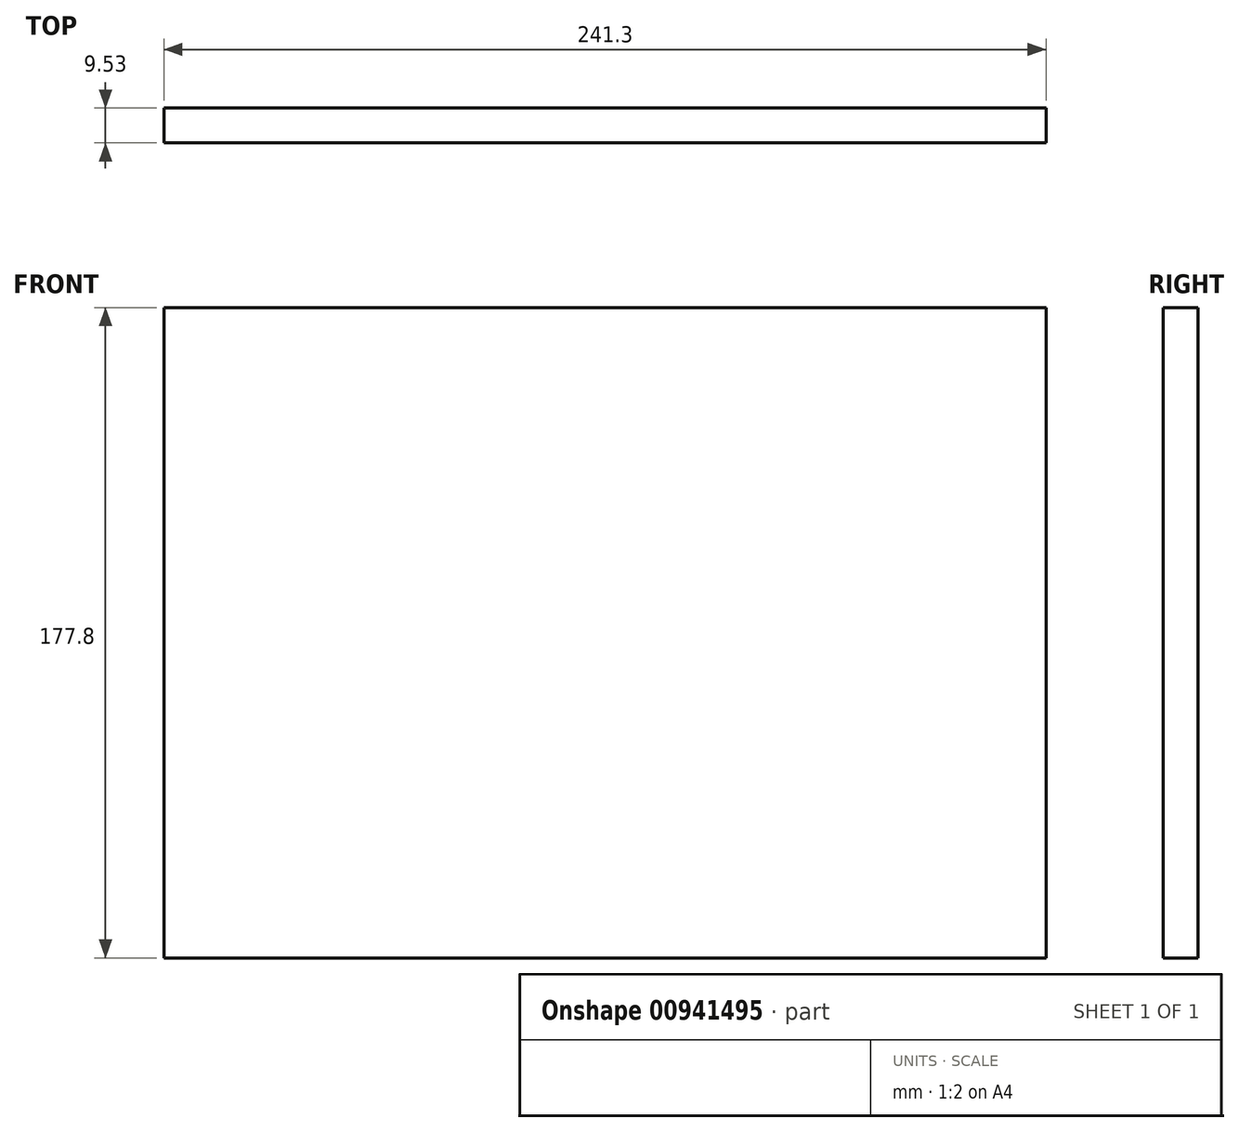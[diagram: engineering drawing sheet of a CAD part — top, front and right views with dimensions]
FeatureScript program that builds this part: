
annotation { "Feature Type Name" : "Feature", "Feature Type Description" : "" }
export const myFeature = defineFeature(function(context is Context, id is Id, definition is map)
    precondition{}
    {
        {
            var Q0;
            Q0=qCreatedBy(makeId("Front.planeOp"),FACE);
            var sketch = newSketch(context, id + "F0", { "sketchPlane" : qUnion([Q0])});
            skLineSegment(sketch, "E0.bottom", {"start": v(120.65, 88.9) * mm, "end": v(-120.65, 88.9) * mm});
            skLineSegment(sketch, "E0.top", {"start": v(120.65, -88.9) * mm, "end": v(-120.65, -88.9) * mm});
            skLineSegment(sketch, "E0.left", {"start": v(120.65, 88.9) * mm, "end": v(120.65, -88.9) * mm});
            skLineSegment(sketch, "E0.right", {"start": v(-120.65, 88.9) * mm, "end": v(-120.65, -88.9) * mm});
            skPoint(sketch, "E0.middle", {"position": v(0, 0) * mm});
            skSolve(sketch);
        }
        {
            var Q0;
            Q0=makeQuery(id+"F0.imprint","IMPRINT",FACE,{"disambiguationData":[TD([[makeQuery(id+"F0.imprint","IMPRINT",EDGE,{"derivedFrom":sQuery(id+"F0.wireOp",EDGE,"E0.bottom")}),1.0]])]});
            var Q1;
            Q1=sQuery(id+"F0.wireOp",EDGE,"E0.bottom");
            var Q2;
            Q2=sQuery(id+"F0.wireOp",EDGE,"E0.right");
            extrude(context, id + "F1", {"entities" : qUnion([Q0]), "surfaceOperationType" : NewSurfaceOperationType.ADD, "surfaceEntities" : qUnion([Q1, Q2]), "depth" : 9.52 * mm, "offsetDistance" : 25.4 * mm});
        }
    });
